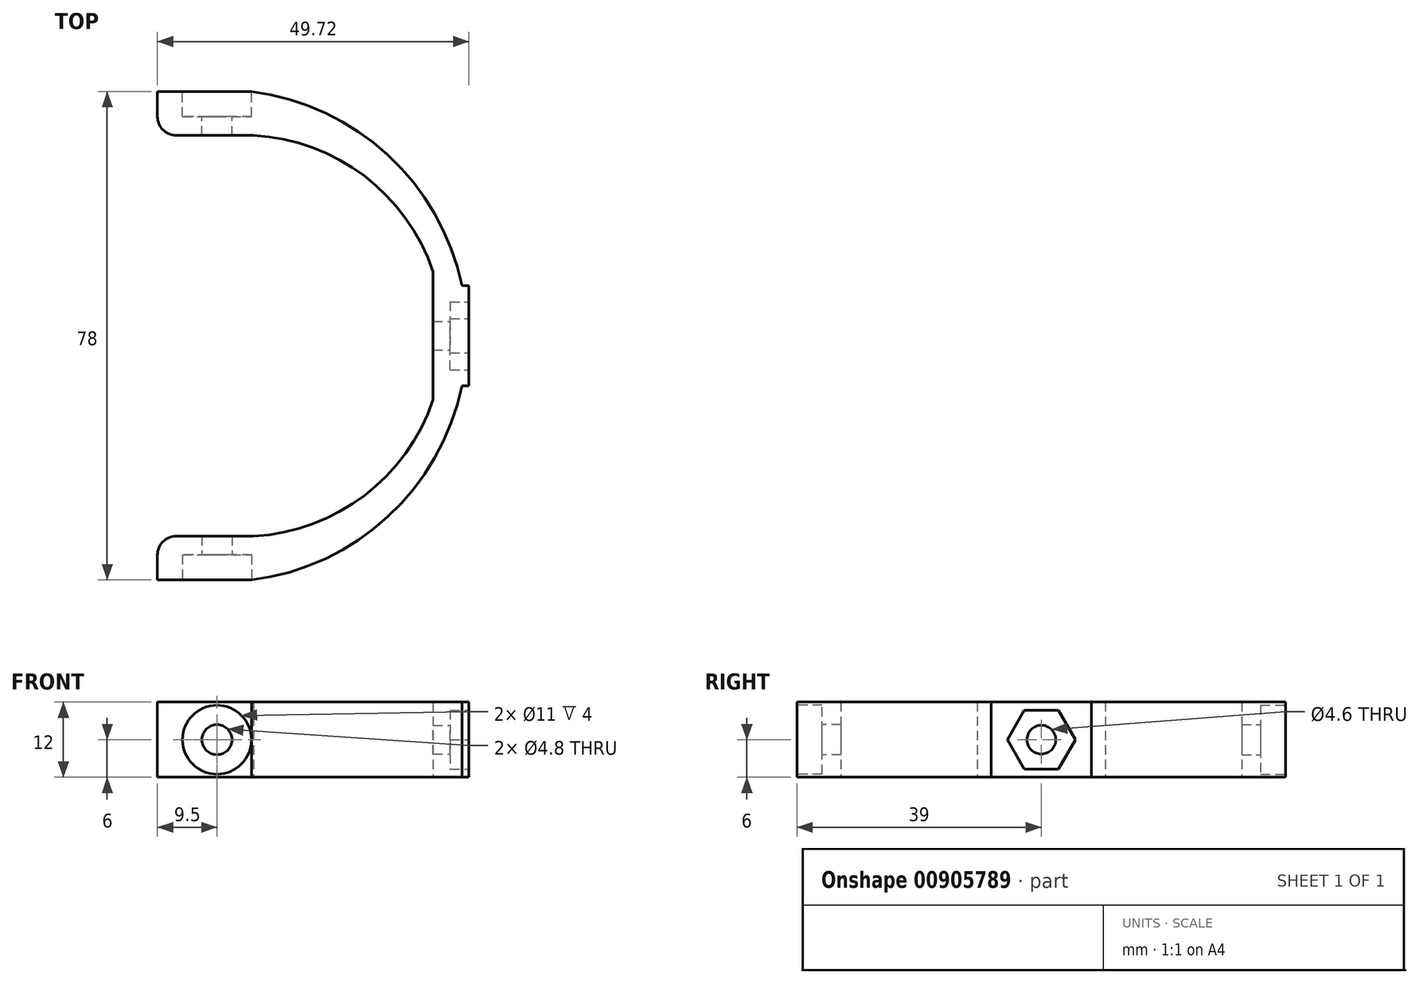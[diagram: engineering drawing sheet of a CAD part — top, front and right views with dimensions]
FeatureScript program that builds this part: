
annotation { "Feature Type Name" : "Feature", "Feature Type Description" : "" }
export const myFeature = defineFeature(function(context is Context, id is Id, definition is map)
    precondition{}
    {
        {
            var Q0;
            Q0=qCreatedBy(makeId("Top.planeOp"),FACE);
            var sketch = newSketch(context, id + "F0", { "sketchPlane" : qUnion([Q0])});
            skLineSegment(sketch, "E0", {"start": v(-6.5, 32) * mm, "end": v(5.86, 32) * mm});
            skLineSegment(sketch, "E1.left", {"start": v(-9.5, 35) * mm, "end": v(-9.5, 39) * mm});
            skLineSegment(sketch, "E2.bottom", {"start": v(-5.5, 35) * mm, "end": v(5.5, 35) * mm});
            skLineSegment(sketch, "E2.left", {"start": v(-5.5, 35) * mm, "end": v(-5.5, 39) * mm});
            skLineSegment(sketch, "E2.right", {"start": v(5.5, 35) * mm, "end": v(5.5, 39) * mm});
            skPoint(sketch, "E2.middle", {"position": v(0, 37) * mm});
            skLineSegment(sketch, "E3.MirrorCS", {"start": v(-5.5, -35) * mm, "end": v(-5.5, -39) * mm});
            skLineSegment(sketch, "E4.MirrorCS", {"start": v(-5.5, -35) * mm, "end": v(5.5, -35) * mm});
            skLineSegment(sketch, "E5.MirrorCS", {"start": v(5.5, -35) * mm, "end": v(5.5, -39) * mm});
            skLineSegment(sketch, "E6", {"start": v(-9.5, 39) * mm, "end": v(5.5, 39) * mm});
            skLineSegment(sketch, "E7.MirrorCS", {"start": v(-9.5, -39) * mm, "end": v(5.5, -39) * mm});
            skLineSegment(sketch, "E8.MirrorCS", {"start": v(-9.5, -35) * mm, "end": v(-9.5, -39) * mm});
            skLineSegment(sketch, "E9.MirrorCS", {"start": v(-6.5, -32) * mm, "end": v(5.86, -32) * mm});
            skArc(sketch, "E10", {"start": v(5.86, -32) * mm, "mid": v(23.53, -25.5) * mm, "end": v(34.5, -10.2) * mm});
            skPoint(sketch, "E11.MirrorCS.end.orphan", {"position": v(5.5, -39) * mm});
            skPoint(sketch, "E11.MirrorCS.start.orphan", {"position": v(5.86, -32) * mm});
            skPoint(sketch, "E12.visualSharp", {"position": v(-9.5, 32) * mm});
            skArc(sketch, "E12.filletArc", {"start": v(-9.5, 35) * mm, "mid": v(-8.62, 32.88) * mm, "end": v(-6.5, 32) * mm});
            skPoint(sketch, "E13.visualSharp", {"position": v(-9.5, -32) * mm});
            skArc(sketch, "E13.filletArc", {"start": v(-6.5, -32) * mm, "mid": v(-8.62, -32.88) * mm, "end": v(-9.5, -35) * mm});
            skArc(sketch, "E14", {"start": v(5.5, -39) * mm, "mid": v(27.27, -28.89) * mm, "end": v(39.1, -8) * mm});
            skPoint(sketch, "E15.middle", {"position": v(36.77, 0) * mm});
            skPoint(sketch, "E15.middle.positionSnap0", {"position": v(36.18, 0) * mm});
            skPoint(sketch, "E15.centerSnap0", {"position": v(36.18, 0) * mm});
            skLineSegment(sketch, "E16", {"start": v(39.1, 8) * mm, "end": v(40.22, 8) * mm});
            skLineSegment(sketch, "E17", {"start": v(40.22, 8) * mm, "end": v(40.22, -8) * mm});
            skLineSegment(sketch, "E18", {"start": v(40.22, -8) * mm, "end": v(39.1, -8) * mm});
            skArc(sketch, "E19.trimOffspring", {"start": v(39.1, 8) * mm, "mid": v(27.27, 28.89) * mm, "end": v(5.5, 39) * mm});
            skArc(sketch, "E20.trimOffspring", {"start": v(34.5, 10.2) * mm, "mid": v(23.53, 25.5) * mm, "end": v(5.86, 32) * mm});
            skLineSegment(sketch, "E21", {"start": v(34.5, 10.2) * mm, "end": v(34.5, -10.2) * mm});
            skPoint(sketch, "E15.top.start.orphan", {"position": v(35.16, 8) * mm});
            skPoint(sketch, "E22.orphan", {"position": v(38.38, 8) * mm});
            skPoint(sketch, "E23.orphan", {"position": v(35.16, -8) * mm});
            skPoint(sketch, "E24.orphan", {"position": v(38.38, -8) * mm});
            skSolve(sketch);
        }
        {
            var Q0;
            Q0=makeQuery(id+"F0.imprint","IMPRINT",FACE,{"disambiguationData":[TD([[makeQuery(id+"F0.imprint","IMPRINT",EDGE,{"derivedFrom":sQuery(id+"F0.wireOp",EDGE,"E2.bottom")}),1.0]])]});
            var Q1;
            Q1=makeQuery(id+"F0.imprint","IMPRINT",FACE,{"disambiguationData":[TD([[makeQuery(id+"F0.imprint","IMPRINT",EDGE,{"derivedFrom":sQuery(id+"F0.wireOp",EDGE,"E0")}),1.0]])]});
            var Q2;
            {var subQ0=sQuery(id+"F0.wireOp",EDGE,"E3.MirrorCS");Q2=makeQuery(id+"F0.imprint","IMPRINT",FACE,{"disambiguationData":[TD([[makeQuery(id+"F0.imprint","IMPRINT",EDGE,{"derivedFrom":subQ0}),1.0]])]});}
            var Q3;
            {var subQ1=sQuery(id+"F0.wireOp",EDGE,"E3.MirrorCS");Q3=makeQuery(id+"F0.imprint","IMPRINT",FACE,{"disambiguationData":[TD([[makeQuery(id+"F0.imprint","IMPRINT",EDGE,{"derivedFrom":subQ1}),-1.0]])]});}
            var Q4;
            {var subQ3=sQuery(id+"F0.wireOp",EDGE,"E15.bottom");Q4=makeQuery(id+"F0.imprint","IMPRINT",FACE,{"disambiguationData":[TD([[makeQuery(id+"F0.imprint","IMPRINT",EDGE,{"derivedFrom":subQ3}),1.0]])]});}
            extrude(context, id + "F1", {"entities" : qUnion([Q0, Q1, Q2, Q3, Q4]), "depth" : 6 * mm, "offsetDistance" : 25 * mm, "hasSecondDirection" : true, "secondDirectionOppositeDirection" : true, "secondDirectionDepth" : 6 * mm});
        }
        {
            var Q0;
            Q0=makeQuery(id+"F1.opExtrude","SWEPT_FACE",FACE,{"disambiguationData":[OSD([sQuery(id+"F0.wireOp",EDGE,"E7.MirrorCS")])]});
            var sketch = newSketch(context, id + "F2", { "sketchPlane" : qUnion([Q0])});
            skCircle(sketch, "E25", {"center": v(0, 0) * mm, "radius": 5.5 * mm});
            skCircle(sketch, "E26", {"center": v(0, 0) * mm, "radius": 2.4 * mm});
            skSolve(sketch);
        }
        {
            var Q0;
            Q0=makeQuery(id+"F2.imprint","IMPRINT",FACE,{"disambiguationData":[TD([[makeQuery(id+"F2.imprint","IMPRINT",EDGE,{"derivedFrom":sQuery(id+"F2.wireOp",EDGE,"E25")}),1.0]])]});
            extrude(context, id + "F3", {"entities" : qUnion([Q0]), "operationType" : NewBodyOperationType.REMOVE, "oppositeDirection" : true, "depth" : 4 * mm, "offsetDistance" : 25 * mm});
        }
        {
            var Q0;
            Q0=makeQuery(id+"F3.boolean.opBoolean","SPLIT",FACE,{"disambiguationData":[TD([makeQuery(id+"F3.opExtrude","SWEPT_FACE",FACE,{"disambiguationData":[OSD([sQuery(id+"F2.wireOp",EDGE,"E26")])]})])],"derivedFrom":makeQuery(id+"F1.opExtrude","SWEPT_FACE",FACE,{"disambiguationData":[OSD([sQuery(id+"F0.wireOp",EDGE,"E7.MirrorCS")])]})});
            extrude(context, id + "F4", {"entities" : qUnion([Q0]), "operationType" : NewBodyOperationType.REMOVE, "oppositeDirection" : true, "depth" : 10.8 * mm, "offsetDistance" : 25 * mm});
        }
        {
            var Q0;
            Q0=makeQuery(id+"F1.opExtrude","SWEPT_FACE",FACE,{"disambiguationData":[OSD([sQuery(id+"F0.wireOp",EDGE,"E6")])]});
            var sketch = newSketch(context, id + "F5", { "sketchPlane" : qUnion([Q0])});
            skCircle(sketch, "E27", {"center": v(0, 0) * mm, "radius": 5.5 * mm});
            skCircle(sketch, "E28", {"center": v(0, 0) * mm, "radius": 2.4 * mm});
            skSolve(sketch);
        }
        {
            var Q0;
            Q0=makeQuery(id+"F5.imprint","IMPRINT",FACE,{"disambiguationData":[TD([[makeQuery(id+"F5.imprint","IMPRINT",EDGE,{"derivedFrom":sQuery(id+"F5.wireOp",EDGE,"E27")}),1.0]])]});
            extrude(context, id + "F6", {"entities" : qUnion([Q0]), "operationType" : NewBodyOperationType.REMOVE, "oppositeDirection" : true, "depth" : 4 * mm, "offsetDistance" : 25 * mm});
        }
        {
            var Q0;
            Q0=makeQuery(id+"F6.boolean.opBoolean","SPLIT",FACE,{"disambiguationData":[TD([makeQuery(id+"F6.opExtrude","SWEPT_FACE",FACE,{"disambiguationData":[OSD([sQuery(id+"F5.wireOp",EDGE,"E28")])]})])],"derivedFrom":makeQuery(id+"F1.opExtrude","SWEPT_FACE",FACE,{"disambiguationData":[OSD([sQuery(id+"F0.wireOp",EDGE,"E6")])]})});
            extrude(context, id + "F7", {"entities" : qUnion([Q0]), "operationType" : NewBodyOperationType.REMOVE, "oppositeDirection" : true, "depth" : 10 * mm, "offsetDistance" : 25 * mm});
        }
        {
            var Q0;
            Q0=makeQuery(id+"F1.opExtrude","SWEPT_FACE",FACE,{"disambiguationData":[OSD([sQuery(id+"F0.wireOp",EDGE,"E17")])]});
            var sketch = newSketch(context, id + "F8", { "sketchPlane" : qUnion([Q0])});
            skCircle(sketch, "E29.cCircle", {"center": v(0, 0) * mm, "radius": 5.43 * mm, "construction": true});
            skLineSegment(sketch, "E29.0", {"start": v(5.43, 0) * mm, "end": v(2.71, -4.7) * mm});
            skLineSegment(sketch, "E29.1", {"start": v(2.71, -4.7) * mm, "end": v(-2.71, -4.7) * mm});
            skLineSegment(sketch, "E29.2", {"start": v(-2.71, -4.7) * mm, "end": v(-5.43, 0) * mm});
            skLineSegment(sketch, "E29.3", {"start": v(-5.43, 0) * mm, "end": v(-2.71, 4.7) * mm});
            skLineSegment(sketch, "E29.4", {"start": v(-2.71, 4.7) * mm, "end": v(2.71, 4.7) * mm});
            skLineSegment(sketch, "E29.5", {"start": v(2.71, 4.7) * mm, "end": v(5.43, 0) * mm});
            skCircle(sketch, "E30", {"center": v(0, 0) * mm, "radius": 2.3 * mm});
            skSolve(sketch);
        }
        {
            var Q0;
            Q0=makeQuery(id+"F8.imprint","IMPRINT",FACE,{"disambiguationData":[TD([[makeQuery(id+"F8.imprint","IMPRINT",EDGE,{"derivedFrom":sQuery(id+"F8.wireOp",EDGE,"E29.0")}),-1.0]])]});
            extrude(context, id + "F9", {"entities" : qUnion([Q0]), "operationType" : NewBodyOperationType.REMOVE, "oppositeDirection" : true, "depth" : 3 * mm, "offsetDistance" : 25 * mm});
        }
        {
            var Q0;
            Q0=makeQuery(id+"F9.boolean.opBoolean","SPLIT",FACE,{"disambiguationData":[TD([makeQuery(id+"F9.opExtrude","SWEPT_FACE",FACE,{"disambiguationData":[OSD([sQuery(id+"F8.wireOp",EDGE,"E30")])]})])],"derivedFrom":makeQuery(id+"F1.opExtrude","SWEPT_FACE",FACE,{"disambiguationData":[OSD([sQuery(id+"F0.wireOp",EDGE,"E17")])]})});
            extrude(context, id + "F10", {"entities" : qUnion([Q0]), "operationType" : NewBodyOperationType.REMOVE, "oppositeDirection" : true, "depth" : 14 * mm, "offsetDistance" : 25 * mm});
        }
    });
